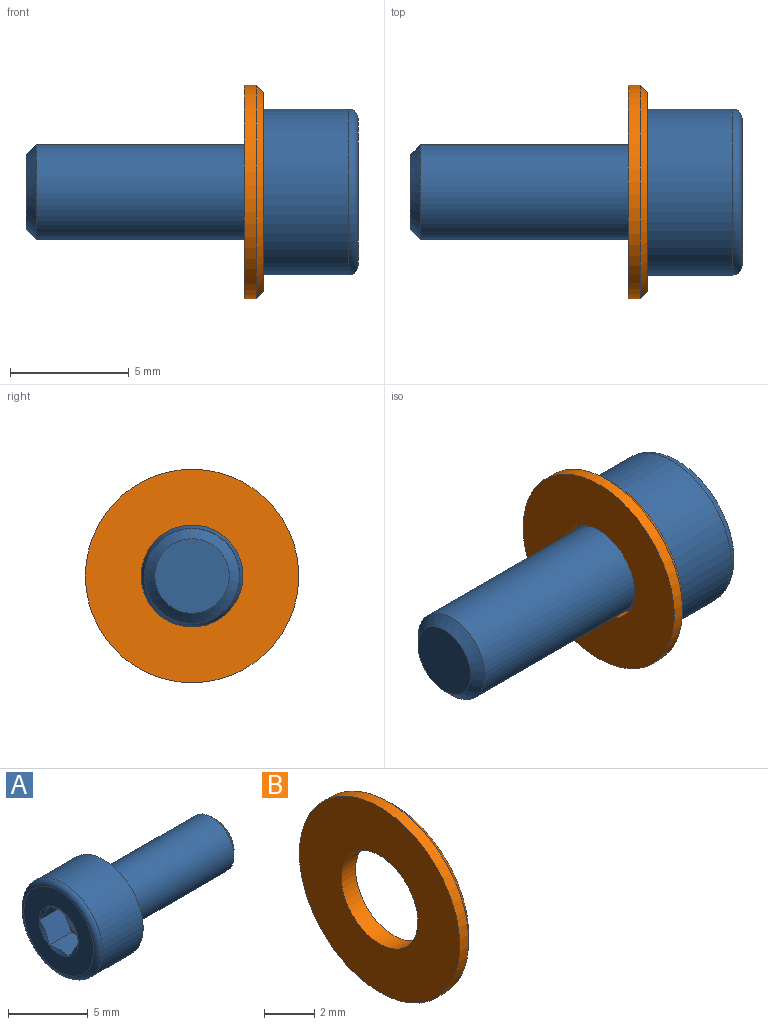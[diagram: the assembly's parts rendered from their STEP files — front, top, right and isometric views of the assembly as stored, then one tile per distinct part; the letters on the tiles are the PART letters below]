
ASSEMBLY  parts=2 mates=1
PART A: 24 faces, bbox 14x7.6x7.6 mm
  f0: plane 1.3x0.75mm, normal (-1,0,0), area 0.1mm2, adj f16,f17,f23
  f1: plane 1.5x0.43mm, normal (-1,0,0), area 0.1mm2, adj f17,f18,f23
  f2: plane 1.3x0.75mm, normal (-1,0,0), area 0.1mm2, adj f18,f19,f23
  f3: plane 1.3x0.75mm, normal (-1,0,0), area 0.1mm2, adj f19,f20,f23
  f4: plane 1.5x0.43mm, normal (-1,0,0), area 0.1mm2, adj f20,f21,f23
  f5: cone r=1.74mm half-angle=60deg, axis (-1,0,0), area 2mm2, adj f15,f16,f17,f18,f19,f20,f21
  f6: cone r=2.01mm half-angle=20.6deg, axis (-1,0,0), area 5.6mm2, adj f7,f11
  f7: torus R=2.2mm, axis (1,0,0), area 0.9mm2, adj f6,f10
  f8: plane 3.14x3.14mm, normal (1,0,0), area 7.7mm2, adj f9
  f9: cone r=2mm half-angle=45deg, axis (-1,0,0), area 6.8mm2, adj f8,f10
  f10: cylinder r=2mm len=8.97mm, axis (1,0,0), area 112.7mm2, adj f7,f9
  f11: torus R=2.35mm, axis (1,0,0), area 3.4mm2, adj f6,f13
  f12: cylinder r=3.5mm len=7mm, axis (1,0,0), area 79.2mm2, adj f13,f14
  f13: plane 7x7mm, normal (1,0,0), area 21.1mm2, adj f11,f12
  f14: torus R=3.1mm, axis (1,0,0), area 13.2mm2, adj f12,f15
  f15: plane 6.2x6.2mm, normal (-1,0,0), area 20.7mm2, adj f5,f14
  f16: plane 2x1.74mm, normal (0,0,-1), area 3.3mm2, adj f0,f5,f17,f21,f22
  f17: plane 2x1.5mm, normal (0,0.87,-0.5), area 3.3mm2, adj f0,f1,f5,f16,f18
  f18: plane 2x1.5mm, normal (0,0.87,0.5), area 3.3mm2, adj f1,f2,f5,f17,f19
  f19: plane 2x1.74mm, normal (0,0,1), area 3.3mm2, adj f2,f3,f5,f18,f20
  f20: plane 2x1.5mm, normal (0,-0.87,0.5), area 3.3mm2, adj f3,f4,f5,f19,f21
  f21: plane 2x1.5mm, normal (0,-0.87,-0.5), area 3.3mm2, adj f4,f5,f16,f20,f22
  f22: plane 1.3x0.75mm, normal (-1,0,0), area 0.1mm2, adj f16,f21,f23
  f23: cone r=1.5mm half-angle=60deg, axis (-1,0,0), area 8.2mm2, adj f0,f1,f2,f3,f4,f22
PART B: 5 faces, bbox 0.8x9x9 mm
  f0: plane 9x9mm, normal (-1,0,0), area 49.1mm2, adj f1,f4
  f1: cylinder r=2.15mm len=4.3mm, axis (1,0,0), area 10.8mm2, adj f0,f2
  f2: plane 8.4x8.4mm, normal (1,0,0), area 40.9mm2, adj f1,f3
  f3: cone r=4.2mm half-angle=45deg, axis (-1,0,0), area 11.6mm2, adj f2,f4
  f4: cylinder r=4.5mm len=9mm, axis (1,0,0), area 14.1mm2, adj f0,f3
PLACE A rot(axis=(0,1,0),180deg) t=(0.8,0,0)mm
PLACE B at identity fixed
MATE fastened A.f5 <-> B.f1  axis (-1,0,0) through (0.8,0,0)mm
